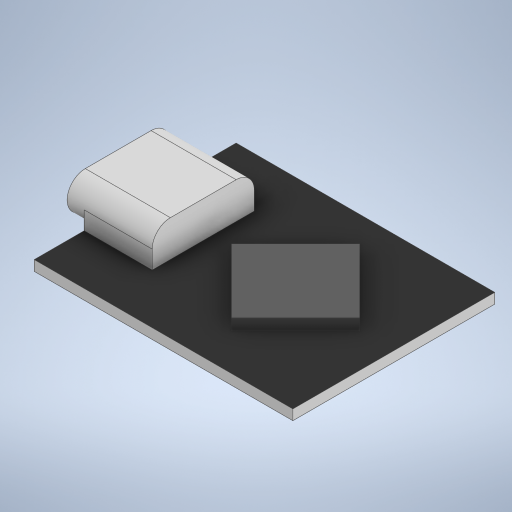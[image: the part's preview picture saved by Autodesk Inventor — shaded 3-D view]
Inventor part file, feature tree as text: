
AUTODESK INVENTOR PART (.ipt)
format: ipt  version: 2023 (Build 270158000, 158)  size: 265,216 bytes
history: native  units: mm
features: extrude x3, sketch x3, fillet x1
ambient origin geometry x8: Origin, YZ Plane, XZ Plane, XY Plane, X Axis, Y Axis, Z Axis, Center Point
bodies: Solid1 (feature_tree)
feature tree (7):
  extrude  "Extrusion1"  Depth=17.8mm
  extrude  "Extrusion2"  TaperAngle=135.0deg  [1 undecoded]
  extrude  "Extrusion3"  Depth=1.6mm
  fillet  "Fillet1"  Radius=1.0mm
  sketch  "Sketch1"  dims[d0=22.8mm d1=17.8mm]
  sketch  "Sketch2"  dims[d2=0.9mm d3=0.0mm d4=135.0deg]
  sketch  "Sketch3"  dims[d5=8.0mm d6=3.0mm d7=1.0mm d8=0.0mm d9=7.5mm d10=1.5mm d11=9.0mm d12=3.2mm d13=0.0mm d14=1.6mm]
note: 1 required parameter value undecoded (feature->parameter linkage not recoverable at this tier; creation-order binding heuristic only, values carry confidence <= 0.55)
